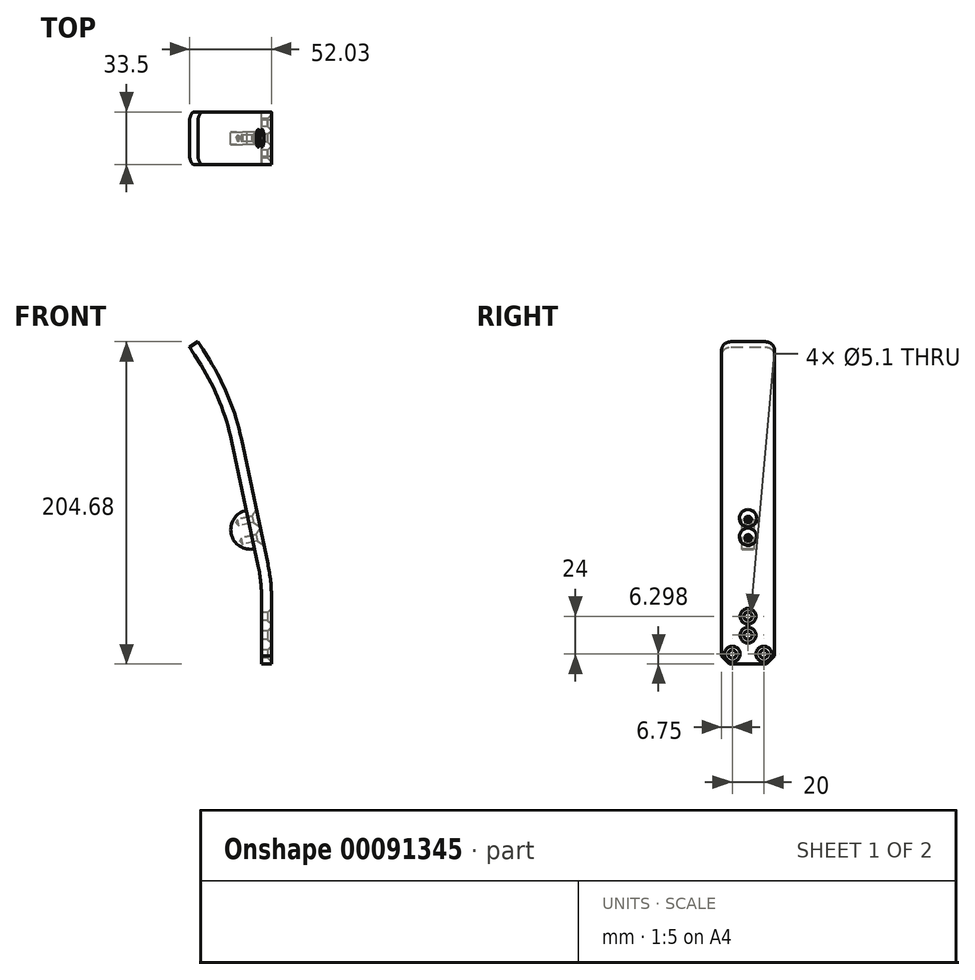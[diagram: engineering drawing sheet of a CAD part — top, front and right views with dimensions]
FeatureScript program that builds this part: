
annotation { "Feature Type Name" : "Feature", "Feature Type Description" : "" }
export const myFeature = defineFeature(function(context is Context, id is Id, definition is map)
    precondition{}
    {
        {
            var Q0;
            Q0=qCreatedBy(makeId("Front.planeOp"),FACE);
            var sketch = newSketch(context, id + "F0", { "sketchPlane" : qUnion([Q0])});
            skLineSegment(sketch, "E0", {"start": v(0, -66.93) * mm, "end": v(0, -25.44) * mm});
            skLineSegment(sketch, "E1", {"start": v(-2.19, -4.65) * mm, "end": v(-19.03, 74.62) * mm});
            skLineSegment(sketch, "E2", {"start": v(-38.55, 122.92) * mm, "end": v(-45.73, 134.41) * mm});
            skPoint(sketch, "E3.visualSharp", {"position": v(0, -14.93) * mm});
            skArc(sketch, "E3.filletArc", {"start": v(0, -25.44) * mm, "mid": v(-0.55, -14.99) * mm, "end": v(-2.19, -4.65) * mm});
            skPoint(sketch, "E4.visualSharp", {"position": v(-24.53, 100.49) * mm});
            skArc(sketch, "E4.filletArc", {"start": v(-19.03, 74.62) * mm, "mid": v(-26.68, 99.62) * mm, "end": v(-38.55, 122.92) * mm});
            skLineSegment(sketch, "E5.0", {"start": v(-33.2, 126.26) * mm, "end": v(-40.39, 137.75) * mm});
            skLineSegment(sketch, "E5.1", {"start": v(6.3, -66.93) * mm, "end": v(6.3, -25.44) * mm});
            skArc(sketch, "E5.2", {"start": v(6.3, -25.44) * mm, "mid": v(5.72, -14.33) * mm, "end": v(3.98, -3.34) * mm});
            skLineSegment(sketch, "E5.3", {"start": v(3.98, -3.34) * mm, "end": v(-12.87, 75.93) * mm});
            skArc(sketch, "E5.4", {"start": v(-12.87, 75.93) * mm, "mid": v(-20.84, 101.98) * mm, "end": v(-33.2, 126.26) * mm});
            skLineSegment(sketch, "E6", {"start": v(-45.73, 134.41) * mm, "end": v(-40.39, 137.75) * mm});
            skLineSegment(sketch, "E7", {"start": v(0, -66.93) * mm, "end": v(6.3, -66.93) * mm});
            skSolve(sketch);
        }
        {
            var Q0;
            Q0=makeQuery(id+"F0.imprint","IMPRINT",FACE,{"disambiguationData":[TD([[makeQuery(id+"F0.imprint","IMPRINT",EDGE,{"derivedFrom":sQuery(id+"F0.wireOp",EDGE,"E0")}),-1.0]])]});
            extrude(context, id + "F1", {"entities" : qUnion([Q0]), "depth" : 33.5 * mm});
        }
        {
            var Q0;
            Q0=makeQuery(id+"F1.opExtrude","CAP_EDGE",EDGE,{"disambiguationData":[OSD([sQuery(id+"F0.wireOp",EDGE,"E6")])],"isStart":false});
            var Q1;
            Q1=makeQuery(id+"F1.opExtrude","CAP_EDGE",EDGE,{"disambiguationData":[OSD([sQuery(id+"F0.wireOp",EDGE,"E6")])],"isStart":true});
            fillet(context, id + "F2", {"entities" : qUnion([Q0, Q1]), "radius" : 6 * mm, "tangentPropagation" : true, "allowEdgeOverflow" : false});
        }
        {
            var Q0;
            Q0=makeQuery(id+"F1.opExtrude","SWEPT_FACE",FACE,{"disambiguationData":[OSD([sQuery(id+"F0.wireOp",EDGE,"E5.1")])]});
            var sketch = newSketch(context, id + "F3", { "sketchPlane" : qUnion([Q0])});
            skSolve(sketch);
        }
        {
            var Q0;
            {var subQ0=sQuery(id+"F0.wireOp",EDGE,"E5.1");Q0=makeQuery(id+"F3.imprint","IMPRINT",FACE,{"disambiguationData":[TD([[makeQuery(id+"F3.imprint","IMPRINT",EDGE,{"derivedFrom":makeQuery(id+"F1.opExtrude","CAP_EDGE",EDGE,{"disambiguationData":[OSD([subQ0])],"isStart":true})}),1.0]])]});}
            var sketch = newSketch(context, id + "F4", { "sketchPlane" : qUnion([Q0])});
            skLineSegment(sketch, "E8", {"start": v(-16.75, -63.48) * mm, "end": v(-16.75, -33.79) * mm, "construction": true});
            skCircle(sketch, "E9", {"center": v(-16.75, -36.63) * mm, "radius": 2.55 * mm});
            skCircle(sketch, "E10", {"center": v(-16.75, -48.63) * mm, "radius": 2.55 * mm});
            skCircle(sketch, "E11", {"center": v(-26.75, -60.63) * mm, "radius": 2.55 * mm});
            skCircle(sketch, "E12.MirrorC", {"center": v(-6.75, -60.63) * mm, "radius": 2.55 * mm});
            skSolve(sketch);
        }
        {
            var Q0;
            Q0=makeQuery(id+"F1.opExtrude","CAP_EDGE",EDGE,{"disambiguationData":[OSD([sQuery(id+"F0.wireOp",EDGE,"E7")])],"isStart":false});
            var Q1;
            Q1=makeQuery(id+"F1.opExtrude","CAP_EDGE",EDGE,{"disambiguationData":[OSD([sQuery(id+"F0.wireOp",EDGE,"E7")])],"isStart":true});
            chamfer(context, id + "F5", {"entities" : qUnion([Q0, Q1]), "width" : 5 * mm, "tangentPropagation" : true});
        }
        {
            var Q0;
            Q0=sQuery(id+"F4.wireOp",VERTEX,"E9.center");
            var Q1;
            Q1=sQuery(id+"F4.wireOp",VERTEX,"E10.center");
            var Q2;
            Q2=sQuery(id+"F4.wireOp",VERTEX,"E11.center");
            var Q3;
            Q3=sQuery(id+"F4.wireOp",VERTEX,"E12.MirrorC.center");
            var Q4;
            Q4=makeQuery(id+"F1.opExtrude","SWEPT_BODY",BODY,{"disambiguationData":[OSD([sQuery(id+"F0.wireOp",EDGE,"E0"),sQuery(id+"F0.wireOp",EDGE,"E1"),sQuery(id+"F0.wireOp",EDGE,"E2"),sQuery(id+"F0.wireOp",EDGE,"E3.filletArc"),sQuery(id+"F0.wireOp",EDGE,"E4.filletArc"),sQuery(id+"F0.wireOp",EDGE,"E5.0"),sQuery(id+"F0.wireOp",EDGE,"E5.1"),sQuery(id+"F0.wireOp",EDGE,"E5.2"),sQuery(id+"F0.wireOp",EDGE,"E5.3"),sQuery(id+"F0.wireOp",EDGE,"E5.4"),sQuery(id+"F0.wireOp",EDGE,"E6"),sQuery(id+"F0.wireOp",EDGE,"E7")])]});
            hole(context, id + "F6", {"style" : HoleStyle.C_SINK, "endStyle" : HoleEndStyle.THROUGH, "holeDiameter" : 5.1 * mm, "cSinkDiameter" : 10 * mm, "cSinkAngle" : 90 * degree, "locations" : qUnion([Q0, Q1, Q2, Q3]), "scope" : qUnion([Q4]), "isTappedThrough" : true, "startStyle" : HoleStartStyle.SKETCH});
        }
        {
            var Q0;
            Q0=makeQuery(id+"F1.opExtrude","SWEPT_FACE",FACE,{"disambiguationData":[OSD([sQuery(id+"F0.wireOp",EDGE,"E1")])]});
            var sketch = newSketch(context, id + "F7", { "sketchPlane" : qUnion([Q0])});
            skLineSegment(sketch, "E13.bottom", {"start": v(12.75, 7) * mm, "end": v(20.75, 7) * mm});
            skLineSegment(sketch, "E13.top", {"start": v(12.75, 32) * mm, "end": v(20.75, 32) * mm});
            skLineSegment(sketch, "E13.left", {"start": v(12.75, 7) * mm, "end": v(12.75, 32) * mm});
            skLineSegment(sketch, "E13.right", {"start": v(20.75, 7) * mm, "end": v(20.75, 32) * mm});
            skLineSegment(sketch, "E14", {"start": v(0, 0) * mm, "end": v(33.5, 0) * mm, "construction": true});
            skLineSegment(sketch, "E15", {"start": v(33.5, 0) * mm, "end": v(0, 0) * mm, "construction": true});
            skLineSegment(sketch, "E16", {"start": v(0, 60.57) * mm, "end": v(0, 0) * mm, "construction": true});
            skSolve(sketch);
        }
        {
            var Q0;
            Q0=makeQuery(id+"F7.imprint","IMPRINT",FACE,{"disambiguationData":[TD([[makeQuery(id+"F7.imprint","IMPRINT",EDGE,{"derivedFrom":sQuery(id+"F7.wireOp",EDGE,"E13.bottom")}),1.0]])]});
            extrude(context, id + "F8", {"entities" : qUnion([Q0]), "operationType" : NewBodyOperationType.ADD, "depth" : 12.5 * mm});
        }
        {
            var Q0;
            Q0=makeQuery(id+"F8.opExtrude","CAP_EDGE",EDGE,{"disambiguationData":[OSD([sQuery(id+"F7.wireOp",EDGE,"E13.bottom")])],"isStart":false});
            var Q1;
            Q1=makeQuery(id+"F8.opExtrude","CAP_EDGE",EDGE,{"disambiguationData":[OSD([sQuery(id+"F7.wireOp",EDGE,"E13.top")])],"isStart":false});
            fillet(context, id + "F9", {"entities" : qUnion([Q0, Q1]), "radius" : 12.5 * mm, "tangentPropagation" : true, "allowEdgeOverflow" : false});
        }
        {
            var Q0;
            Q0=makeQuery(id+"F7.imprint","IMPRINT",FACE,{"disambiguationData":[TD([[makeQuery(id+"F7.imprint","IMPRINT",EDGE,{"derivedFrom":sQuery(id+"F7.wireOp",EDGE,"E13.bottom")}),-1.0]])]});
            cPlane(context, id + "F10", {"entities" : qUnion([Q0]), "cplaneType" : CPlaneType.OFFSET, "offset" : 6.3 * mm, "oppositeDirection" : true, "width" : 150 * mm, "height" : 150 * mm});
        }
        {
            var Q0;
            Q0=qCreatedBy(id+"F10.planeOp",FACE);
            var sketch = newSketch(context, id + "F11", { "sketchPlane" : qUnion([Q0])});
            skPoint(sketch, "E17.0", {"position": v(12.75, 32) * mm});
            skPoint(sketch, "E18.0", {"position": v(20.75, 32) * mm});
            skPoint(sketch, "E19.0", {"position": v(12.75, 7) * mm});
            skPoint(sketch, "E20.0", {"position": v(20.75, 7) * mm});
            skLineSegment(sketch, "E21", {"start": v(12.75, 32) * mm, "end": v(20.75, 32) * mm, "construction": true});
            skLineSegment(sketch, "E22", {"start": v(12.75, 7) * mm, "end": v(20.75, 7) * mm, "construction": true});
            skLineSegment(sketch, "E23", {"start": v(12.75, 32) * mm, "end": v(12.75, 7) * mm, "construction": true});
            skLineSegment(sketch, "E24", {"start": v(20.75, 7) * mm, "end": v(20.75, 32) * mm, "construction": true});
            skLineSegment(sketch, "E25", {"start": v(12.75, 19.5) * mm, "end": v(20.75, 19.5) * mm, "construction": true});
            skLineSegment(sketch, "E26", {"start": v(16.75, 32) * mm, "end": v(16.75, 7) * mm, "construction": true});
            skLineSegment(sketch, "E27.0", {"start": v(12.75, 13.5) * mm, "end": v(20.75, 13.5) * mm, "construction": true});
            skLineSegment(sketch, "E28.0", {"start": v(12.75, 25.5) * mm, "end": v(20.75, 25.5) * mm, "construction": true});
            skPoint(sketch, "E29", {"position": v(16.75, 25.5) * mm});
            skPoint(sketch, "E30", {"position": v(16.75, 13.5) * mm});
            skSolve(sketch);
        }
        {
            var Q0;
            Q0=sQuery(id+"F11.wireOp",VERTEX,"E29");
            var Q1;
            Q1=sQuery(id+"F11.wireOp",VERTEX,"E30");
            var Q2;
            Q2=makeQuery(id+"F1.opExtrude","SWEPT_BODY",BODY,{"disambiguationData":[OSD([sQuery(id+"F0.wireOp",EDGE,"E0"),sQuery(id+"F0.wireOp",EDGE,"E1"),sQuery(id+"F0.wireOp",EDGE,"E2"),sQuery(id+"F0.wireOp",EDGE,"E3.filletArc"),sQuery(id+"F0.wireOp",EDGE,"E4.filletArc"),sQuery(id+"F0.wireOp",EDGE,"E5.0"),sQuery(id+"F0.wireOp",EDGE,"E5.1"),sQuery(id+"F0.wireOp",EDGE,"E5.2"),sQuery(id+"F0.wireOp",EDGE,"E5.3"),sQuery(id+"F0.wireOp",EDGE,"E5.4"),sQuery(id+"F0.wireOp",EDGE,"E6"),sQuery(id+"F0.wireOp",EDGE,"E7")])]});
            hole(context, id + "F12", {"style" : HoleStyle.C_SINK, "endStyle" : HoleEndStyle.BLIND, "oppositeDirection" : true, "standardTappedOrClearance" : lookupTablePath({ "standard" : "ISO", "size" : "4.2", "type" : "Drilled" }), "standardBlindInLast" : lookupTablePath({ "standard" : "ISO", "size" : "4.2", "type" : "Drilled" }), "holeDiameter" : 4.2 * mm, "cSinkDiameter" : 11.2 * mm, "cSinkAngle" : 90 * degree, "holeDepth" : 13 * mm, "locations" : qUnion([Q0, Q1]), "scope" : qUnion([Q2]), "startStyle" : HoleStartStyle.SKETCH});
        }
    });
